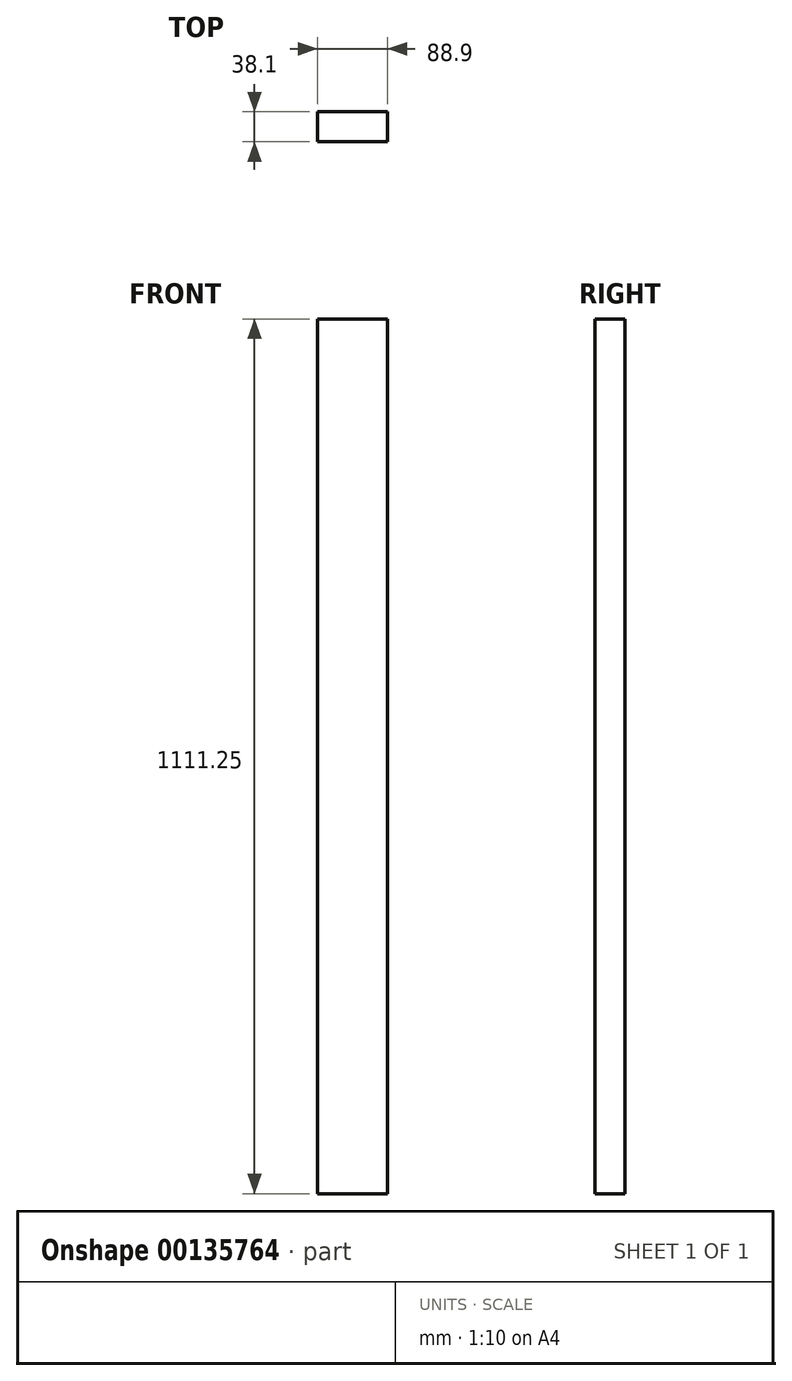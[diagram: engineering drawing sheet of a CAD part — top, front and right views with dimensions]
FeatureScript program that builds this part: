
annotation { "Feature Type Name" : "Feature", "Feature Type Description" : "" }
export const myFeature = defineFeature(function(context is Context, id is Id, definition is map)
    precondition{}
    {
        {
            var Q0;
            Q0=qCreatedBy(makeId("Front.planeOp"),FACE);
            var sketch = newSketch(context, id + "F0", { "sketchPlane" : qUnion([Q0])});
            skLineSegment(sketch, "E0.bottom", {"start": v(0, 0) * mm, "end": v(88.9, 0) * mm});
            skLineSegment(sketch, "E0.top", {"start": v(0, 1111.25) * mm, "end": v(88.9, 1111.25) * mm});
            skLineSegment(sketch, "E0.left", {"start": v(0, 0) * mm, "end": v(0, 1111.25) * mm});
            skLineSegment(sketch, "E0.right", {"start": v(88.9, 0) * mm, "end": v(88.9, 1111.25) * mm});
            skSolve(sketch);
        }
        {
            var Q0;
            Q0=makeQuery(id+"F0.imprint","IMPRINT",FACE,{"disambiguationData":[TD([[makeQuery(id+"F0.imprint","IMPRINT",EDGE,{"derivedFrom":sQuery(id+"F0.wireOp",EDGE,"E0.bottom")}),1.0]])]});
            extrude(context, id + "F1", {"entities" : qUnion([Q0]), "depth" : 38.1 * mm});
        }
    });
